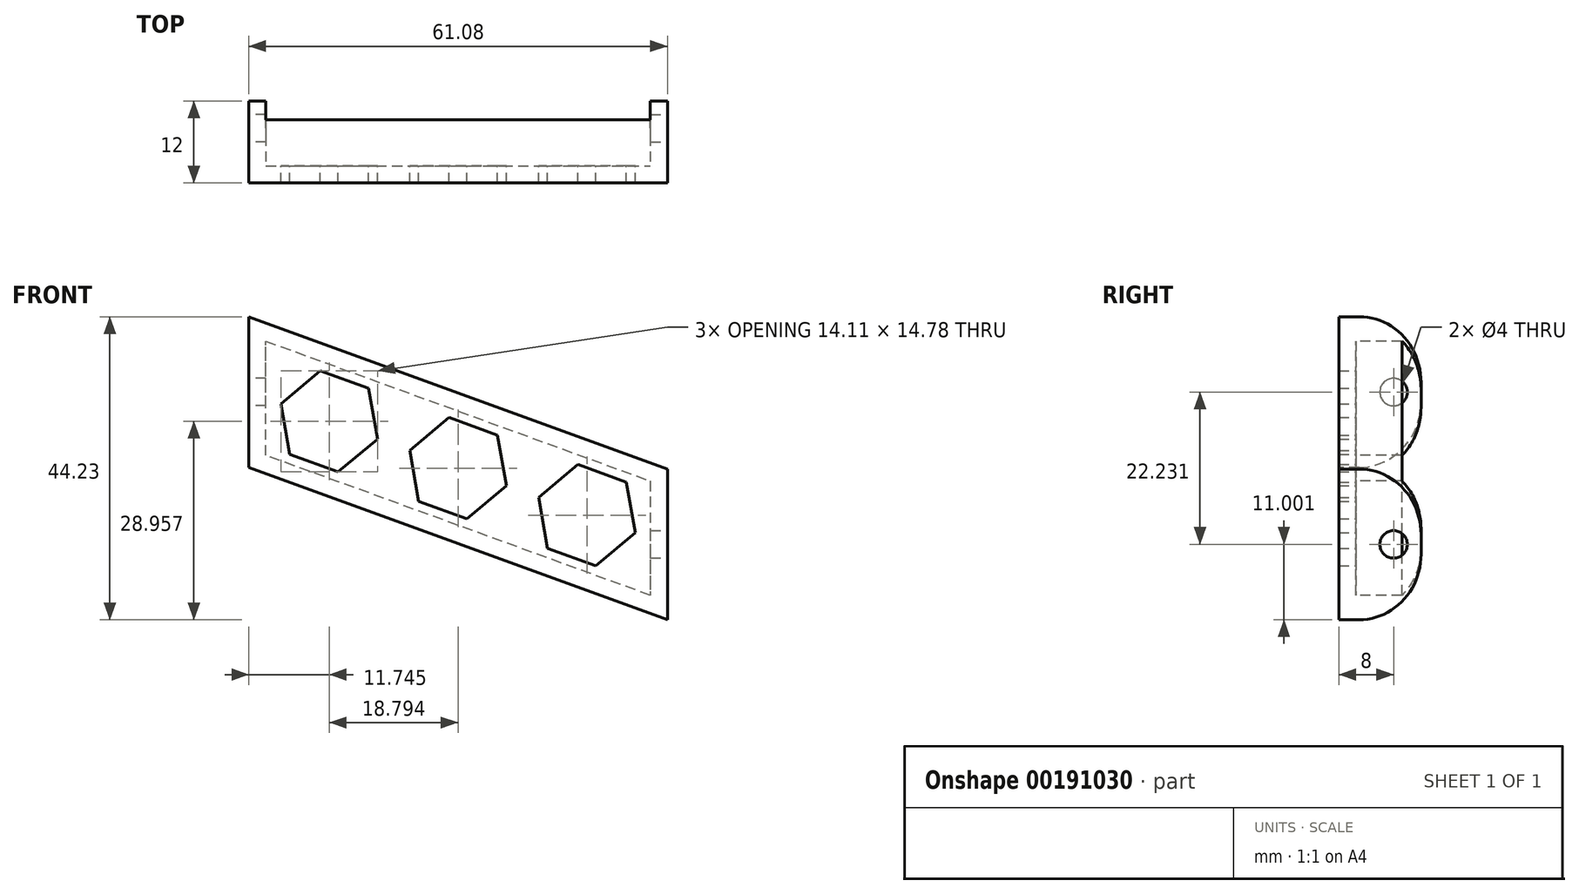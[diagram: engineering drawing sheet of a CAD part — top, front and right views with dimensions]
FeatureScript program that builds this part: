
annotation { "Feature Type Name" : "Feature", "Feature Type Description" : "" }
export const myFeature = defineFeature(function(context is Context, id is Id, definition is map)
    precondition{}
    {
        {
            var Q0;
            Q0=qCreatedBy(makeId("Front.planeOp"),FACE);
            var sketch = newSketch(context, id + "F0", { "sketchPlane" : qUnion([Q0])});
            skLineSegment(sketch, "E0", {"start": v(-42.31, 32.53) * mm, "end": v(18.77, 10.3) * mm});
            skLineSegment(sketch, "E1", {"start": v(18.77, 10.3) * mm, "end": v(18.77, -11.7) * mm});
            skLineSegment(sketch, "E2", {"start": v(18.77, -11.7) * mm, "end": v(-42.31, 10.53) * mm});
            skLineSegment(sketch, "E3", {"start": v(-42.31, 10.53) * mm, "end": v(-42.31, 32.53) * mm});
            skLineSegment(sketch, "E4", {"start": v(-58.39, -35.96) * mm, "end": v(39.08, -35.96) * mm, "construction": true});
            skLineSegment(sketch, "E5", {"start": v(56.74, 21.01) * mm, "end": v(56.74, -32.43) * mm, "construction": true});
            skLineSegment(sketch, "E6", {"start": v(-11.77, 21.42) * mm, "end": v(-18.84, 2) * mm, "construction": true});
            skLineSegment(sketch, "E7", {"start": v(18.77, -0.7) * mm, "end": v(-42.31, 21.53) * mm, "construction": true});
            skSolve(sketch);
        }
        {
            var Q0;
            Q0=makeQuery(id+"F0.imprint","IMPRINT",FACE,{"disambiguationData":[TD([[makeQuery(id+"F0.imprint","IMPRINT",EDGE,{"derivedFrom":sQuery(id+"F0.wireOp",EDGE,"E0")}),-1.0]])]});
            extrude(context, id + "F1", {"entities" : qUnion([Q0]), "oppositeDirection" : true, "depth" : 12 * mm});
        }
        {
            var Q0;
            Q0=makeQuery(id+"F1.opExtrude","CAP_FACE",FACE,{"disambiguationData":[OSD([sQuery(id+"F0.wireOp",EDGE,"E0"),sQuery(id+"F0.wireOp",EDGE,"E1"),sQuery(id+"F0.wireOp",EDGE,"E2"),sQuery(id+"F0.wireOp",EDGE,"E3")])],"isStart":false});
            shell(context, id + "F2", {"entities" : qUnion([Q0]), "thickness" : 2.5 * mm});
        }
        {
            var Q0;
            Q0=makeQuery(id+"F1.opExtrude","SWEPT_FACE",FACE,{"disambiguationData":[OSD([sQuery(id+"F0.wireOp",EDGE,"E1")])]});
            var sketch = newSketch(context, id + "F3", { "sketchPlane" : qUnion([Q0])});
            skLineSegment(sketch, "E8", {"start": v(12, -0.7) * mm, "end": v(0, -0.7) * mm, "construction": true});
            skPoint(sketch, "E9", {"position": v(8, -0.7) * mm});
            skLineSegment(sketch, "E10.bottom", {"start": v(0, 10.3) * mm, "end": v(12, 10.3) * mm});
            skLineSegment(sketch, "E10.top", {"start": v(0, -11.7) * mm, "end": v(12, -11.7) * mm});
            skLineSegment(sketch, "E10.left", {"start": v(0, 10.3) * mm, "end": v(0, -11.7) * mm});
            skLineSegment(sketch, "E10.right", {"start": v(12, 10.3) * mm, "end": v(12, -11.7) * mm});
            skSolve(sketch);
        }
        {
            var Q0;
            Q0=sQuery(id+"F3.wireOp",VERTEX,"E9");
            var Q1;
            Q1=makeQuery(id+"F1.opExtrude","SWEPT_BODY",BODY,{"disambiguationData":[OSD([sQuery(id+"F0.wireOp",EDGE,"E0"),sQuery(id+"F0.wireOp",EDGE,"E1"),sQuery(id+"F0.wireOp",EDGE,"E2"),sQuery(id+"F0.wireOp",EDGE,"E3")])]});
            hole(context, id + "F4", {"style" : HoleStyle.SIMPLE, "endStyle" : HoleEndStyle.BLIND, "holeDiameter" : 4 * mm, "holeDepth" : 6 * mm, "locations" : qUnion([Q0]), "scope" : qUnion([Q1])});
        }
        {
            var Q0;
            Q0=makeQuery(id+"F1.opExtrude","SWEPT_FACE",FACE,{"disambiguationData":[OSD([sQuery(id+"F0.wireOp",EDGE,"E3")])]});
            var sketch = newSketch(context, id + "F5", { "sketchPlane" : qUnion([Q0])});
            skLineSegment(sketch, "E11", {"start": v(-12, 21.53) * mm, "end": v(0, 21.53) * mm, "construction": true});
            skPoint(sketch, "E12", {"position": v(-8, 21.53) * mm});
            skLineSegment(sketch, "E13.bottom", {"start": v(-12, 32.53) * mm, "end": v(0, 32.53) * mm});
            skLineSegment(sketch, "E13.top", {"start": v(-12, 10.53) * mm, "end": v(0, 10.53) * mm});
            skLineSegment(sketch, "E13.left", {"start": v(-12, 32.53) * mm, "end": v(-12, 10.53) * mm});
            skLineSegment(sketch, "E13.right", {"start": v(0, 32.53) * mm, "end": v(0, 10.53) * mm});
            skSolve(sketch);
        }
        {
            var Q0;
            Q0=sQuery(id+"F5.wireOp",VERTEX,"E12");
            var Q1;
            Q1=makeQuery(id+"F1.opExtrude","SWEPT_BODY",BODY,{"disambiguationData":[OSD([sQuery(id+"F0.wireOp",EDGE,"E0"),sQuery(id+"F0.wireOp",EDGE,"E1"),sQuery(id+"F0.wireOp",EDGE,"E2"),sQuery(id+"F0.wireOp",EDGE,"E3")])]});
            hole(context, id + "F6", {"style" : HoleStyle.SIMPLE, "endStyle" : HoleEndStyle.BLIND, "holeDiameter" : 4 * mm, "holeDepth" : 6 * mm, "locations" : qUnion([Q0]), "scope" : qUnion([Q1])});
        }
        {
            var Q0;
            Q0=makeQuery(id+"F2.opShell","OFFSET_FACE",FACE,{"disambiguationData":[OSD([sQuery(id+"F0.wireOp",EDGE,"E0"),sQuery(id+"F0.wireOp",EDGE,"E1"),sQuery(id+"F0.wireOp",EDGE,"E2"),sQuery(id+"F0.wireOp",EDGE,"E3")])]});
            var sketch = newSketch(context, id + "F7", { "sketchPlane" : qUnion([Q0])});
            skCircle(sketch, "E14.cCircle", {"center": v(-7.02, 3.58) * mm, "radius": 6.5 * mm, "construction": true});
            skLineSegment(sketch, "E14.0", {"start": v(0.03, 6.14) * mm, "end": v(-1.27, -1.25) * mm});
            skLineSegment(sketch, "E14.1", {"start": v(-1.27, -1.25) * mm, "end": v(-8.33, -3.82) * mm});
            skLineSegment(sketch, "E14.2", {"start": v(-8.33, -3.82) * mm, "end": v(-14.08, 1) * mm});
            skLineSegment(sketch, "E14.3", {"start": v(-14.08, 1) * mm, "end": v(-12.77, 8.4) * mm});
            skLineSegment(sketch, "E14.4", {"start": v(-12.77, 8.4) * mm, "end": v(-5.72, 10.97) * mm});
            skLineSegment(sketch, "E14.5", {"start": v(-5.72, 10.97) * mm, "end": v(0.03, 6.14) * mm});
            skPoint(sketch, "E14.0.midPoint", {"position": v(-0.62, 2.45) * mm});
            skCircle(sketch, "E15.cCircle", {"center": v(11.77, 10.42) * mm, "radius": 6.5 * mm, "construction": true});
            skLineSegment(sketch, "E15.0", {"start": v(17.52, 5.6) * mm, "end": v(10.47, 3.03) * mm});
            skLineSegment(sketch, "E15.1", {"start": v(10.47, 3.03) * mm, "end": v(4.72, 7.85) * mm});
            skLineSegment(sketch, "E15.2", {"start": v(4.72, 7.85) * mm, "end": v(6.02, 15.24) * mm});
            skLineSegment(sketch, "E15.3", {"start": v(6.02, 15.24) * mm, "end": v(13.07, 17.8) * mm});
            skLineSegment(sketch, "E15.4", {"start": v(13.07, 17.8) * mm, "end": v(18.82, 12.98) * mm});
            skLineSegment(sketch, "E15.5", {"start": v(18.82, 12.98) * mm, "end": v(17.52, 5.6) * mm});
            skCircle(sketch, "E16.cCircle", {"center": v(30.56, 17.26) * mm, "radius": 6.5 * mm, "construction": true});
            skLineSegment(sketch, "E16.0", {"start": v(36.31, 12.43) * mm, "end": v(29.26, 9.87) * mm});
            skLineSegment(sketch, "E16.1", {"start": v(29.26, 9.87) * mm, "end": v(23.51, 14.7) * mm});
            skLineSegment(sketch, "E16.2", {"start": v(23.51, 14.7) * mm, "end": v(24.82, 22.08) * mm});
            skLineSegment(sketch, "E16.3", {"start": v(24.82, 22.08) * mm, "end": v(31.87, 24.65) * mm});
            skLineSegment(sketch, "E16.4", {"start": v(31.87, 24.65) * mm, "end": v(37.62, 19.82) * mm});
            skLineSegment(sketch, "E16.5", {"start": v(37.62, 19.82) * mm, "end": v(36.31, 12.43) * mm});
            skLineSegment(sketch, "E17", {"start": v(-16.27, 0.21) * mm, "end": v(39.81, 20.62) * mm, "construction": true});
            skLineSegment(sketch, "E18", {"start": v(39.81, 20.62) * mm, "end": v(11.77, 18.09) * mm, "construction": true});
            skPoint(sketch, "E18.endSnap0", {"position": v(11.77, 18.76) * mm});
            skLineSegment(sketch, "E19", {"start": v(11.77, 18.09) * mm, "end": v(11.77, 2.08) * mm, "construction": true});
            skSolve(sketch);
        }
        {
            var Q0;
            Q0 = qSketchRegion(id + "F7", true);
            extrude(context, id + "F8", {"entities" : qUnion([Q0]), "operationType" : NewBodyOperationType.REMOVE, "oppositeDirection" : true, "depth" : 25 * mm});
        }
        {
            var Q0;
            Q0=makeQuery(id+"F1.opExtrude","CAP_EDGE",EDGE,{"disambiguationData":[OSD([sQuery(id+"F0.wireOp",EDGE,"E0")])],"isStart":false});
            var Q1;
            Q1=makeQuery(id+"F1.opExtrude","CAP_EDGE",EDGE,{"disambiguationData":[OSD([sQuery(id+"F0.wireOp",EDGE,"E2")])],"isStart":false});
            fillet(context, id + "F9", {"entities" : qUnion([Q0, Q1]), "radius" : 9 * mm, "tangentPropagation" : true, "allowEdgeOverflow" : false});
        }
    });
